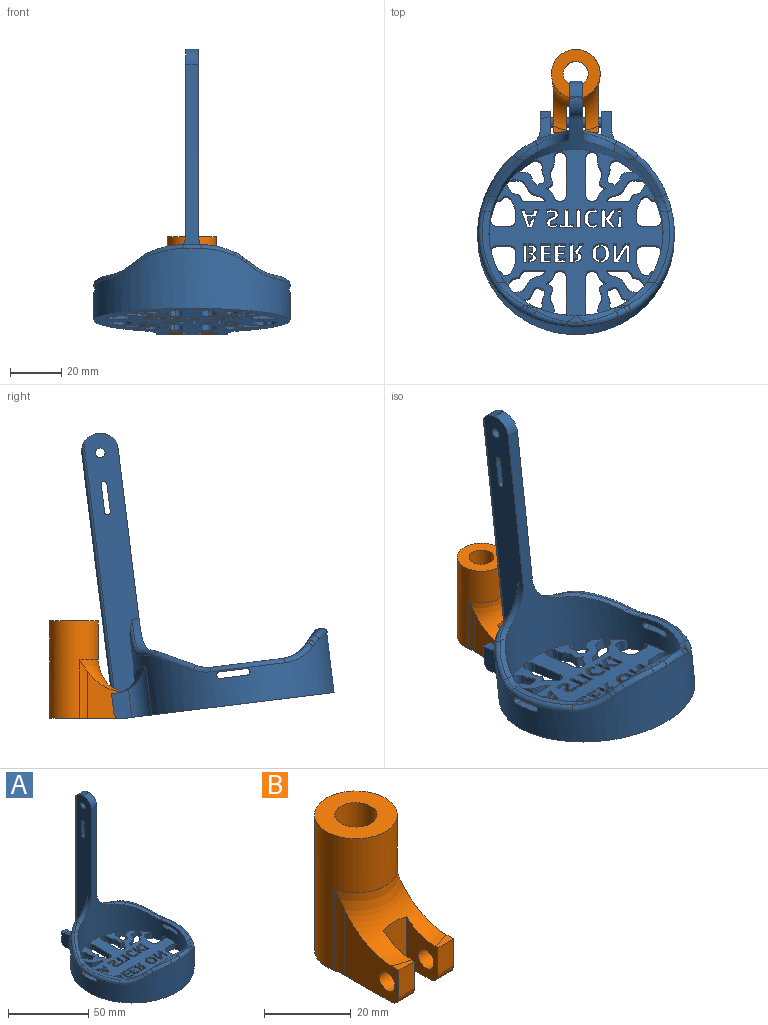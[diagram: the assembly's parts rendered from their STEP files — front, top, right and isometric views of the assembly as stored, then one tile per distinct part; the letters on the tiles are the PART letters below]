
ASSEMBLY  parts=2 mates=1
PART A: 362 faces, bbox 83.9x98.5x112.5 mm
  f0: plane 112.23x13.52mm, normal (-1,0,0), area 1224.4mm2, adj f3,f247,f253,f287,f289,f299,f302,f305
  f1: plane 112.23x13.52mm, normal (1,0,0), area 1226.5mm2, adj f3,f247,f253,f287,f296,f297,f298,f305
  f2: plane 6.78x2.6mm, normal (0,0,1), area 8.5mm2, adj f314,f320,f335
  f3: cylinder r=38.42mm len=76.84mm, axis (0,0,-1), area 3852.1mm2, adj f0,f1,f253,f297,f302,f303,f304,f326
  f4: plane 68.07x68.07mm, normal (0,0,1), area 2117.4mm2, adj f5,f6,f7,f8,f9,f10,f11,f12
  f5: extruded ~6.43x3.81mm, area 32.9mm2, adj f4,f225,f253,f283
  f6: extruded ~6.43x3.81mm, area 32.9mm2, adj f4,f7,f253,f282
  f7: extruded ~7.59x5.02mm, area 38.4mm2, adj f4,f6,f247,f253
  f8: extruded ~7.59x5.02mm, area 38.4mm2, adj f4,f226,f247,f253
  f9: extruded ~3.81x0.62mm, area 2.6mm2, adj f4,f10,f227,f253
  f10: extruded ~3.81x0.62mm, area 2.6mm2, adj f4,f9,f11,f253
  f11: extruded ~3.81x0.64mm, area 2.6mm2, adj f4,f10,f12,f253
  f12: extruded ~3.81x0.63mm, area 2.6mm2, adj f4,f11,f13,f253
  f13: extruded ~3.81x0.61mm, area 2.6mm2, adj f4,f12,f14,f253
  f14: extruded ~3.81x0.62mm, area 2.6mm2, adj f4,f13,f15,f253
  f15: extruded ~3.81x0.63mm, area 2.6mm2, adj f4,f14,f227,f253
  f16: plane 3.81x1.2mm, normal (0,-1,0), area 4.6mm2, adj f4,f17,f228,f253
  f17: plane 4.8x3.81mm, normal (-1,-0.05,0), area 18.3mm2, adj f4,f16,f18,f253
  f18: plane 3.81x1.7mm, normal (0,1,0), area 6.5mm2, adj f4,f17,f228,f253
  f19: plane 3.81x1.73mm, normal (0,-1,0), area 6.6mm2, adj f4,f20,f229,f253
  f20: plane 4x3.81mm, normal (-0.85,0.53,0), area 18mm2, adj f4,f19,f21,f253
  f21: plane 3.81x3.18mm, normal (-0.79,-0.62,0), area 15.4mm2, adj f4,f20,f22,f253
  f22: plane 3.81x1.69mm, normal (0,1,0), area 6.4mm2, adj f4,f21,f23,f253
  f23: plane 3.81x2.44mm, normal (0.78,0.62,0), area 11.9mm2, adj f4,f22,f24,f253
  f24: plane 3.81x0.85mm, normal (0.82,0.58,0), area 3.9mm2, adj f4,f23,f25,f253
  f25: plane 3.81x3.28mm, normal (-1,0,0), area 12.5mm2, adj f4,f24,f26,f253
  f26: plane 3.81x1.52mm, normal (0,1,0), area 5.8mm2, adj f4,f25,f27,f253
  f27: plane 7.18x3.81mm, normal (1,0,0), area 27.3mm2, adj f4,f26,f28,f253
  f28: plane 3.81x1.52mm, normal (0,-1,0), area 5.8mm2, adj f4,f27,f29,f253
  f29: plane 3.81x2.56mm, normal (-1,0,0), area 9.8mm2, adj f4,f28,f30,f253
  f30: plane 3.81x0.64mm, normal (-0.58,-0.81,0), area 3mm2, adj f4,f29,f229,f253
  f31: extruded ~3.81x1.33mm, area 5.9mm2, adj f4,f32,f230,f253
  f32: extruded ~3.81x0.8mm, area 3.1mm2, adj f4,f31,f33,f253
  f33: extruded ~3.81x0.81mm, area 3.3mm2, adj f4,f32,f34,f253
  f34: plane 3.81x1.24mm, normal (-0.93,-0.37,0), area 5.1mm2, adj f4,f33,f35,f253
  f35: extruded ~3.81x2.1mm, area 8.3mm2, adj f4,f34,f36,f253
  f36: extruded ~3.81x1.79mm, area 7.1mm2, adj f4,f35,f37,f253
  f37: extruded ~3.81x1.29mm, area 6.7mm2, adj f4,f36,f38,f253
  f38: extruded ~3.81x1.96mm, area 7.7mm2, adj f4,f37,f39,f253
  f39: extruded ~3.81x2.73mm, area 11.1mm2, adj f4,f38,f40,f253
  f40: extruded ~3.81x2.4mm, area 10.1mm2, adj f4,f39,f41,f253
  f41: extruded ~3.81x1.97mm, area 7.7mm2, adj f4,f40,f42,f253
  f42: plane 3.81x1.28mm, normal (-1,0,0), area 4.9mm2, adj f4,f41,f43,f253
  f43: extruded ~3.81x1.83mm, area 7.1mm2, adj f4,f42,f44,f253
  f44: extruded ~3.81x2.4mm, area 13mm2, adj f4,f43,f230,f253
  f45: plane 7.18x3.81mm, normal (1,0,0), area 27.3mm2, adj f4,f46,f231,f253
  f46: plane 3.81x1.52mm, normal (0,-1,0), area 5.8mm2, adj f4,f45,f47,f253
  f47: plane 7.18x3.81mm, normal (-1,0,0), area 27.3mm2, adj f4,f46,f231,f253
  f48: plane 3.81x1.52mm, normal (0,-1,0), area 5.8mm2, adj f4,f49,f232,f253
  f49: plane 5.91x3.81mm, normal (-1,0,0), area 22.5mm2, adj f4,f48,f50,f253
  f50: plane 3.81x1.95mm, normal (0,-1,0), area 7.4mm2, adj f4,f49,f51,f253
  f51: plane 3.81x1.27mm, normal (-1,0,0), area 4.8mm2, adj f4,f50,f52,f253
  f52: plane 5.42x3.81mm, normal (0,1,0), area 20.6mm2, adj f4,f51,f53,f253
  f53: plane 3.81x1.27mm, normal (1,0,0), area 4.8mm2, adj f4,f52,f54,f253
  f54: plane 3.81x1.95mm, normal (0,-1,0), area 7.4mm2, adj f4,f53,f232,f253
  f55: extruded ~3.81x1.53mm, area 6.7mm2, adj f4,f56,f233,f253
  f56: extruded ~3.81x1.19mm, area 4.8mm2, adj f4,f55,f57,f253
  f57: extruded ~3.81x1.38mm, area 6.5mm2, adj f4,f56,f58,f253
  f58: extruded ~3.81x0.96mm, area 4.1mm2, adj f4,f57,f59,f253
  f59: extruded ~3.81x0.3mm, area 1.6mm2, adj f4,f58,f60,f253
  f60: extruded ~3.81x0.35mm, area 1.4mm2, adj f4,f59,f61,f253
  f61: extruded ~3.81x0.52mm, area 2.3mm2, adj f4,f60,f62,f253
  f62: extruded ~3.81x0.66mm, area 2.7mm2, adj f4,f61,f63,f253
  f63: extruded ~3.81x0.74mm, area 2.8mm2, adj f4,f62,f64,f253
  f64: extruded ~3.81x0.95mm, area 3.8mm2, adj f4,f63,f65,f253
  f65: plane 3.81x1.18mm, normal (-0.92,-0.38,0), area 4.9mm2, adj f4,f64,f66,f253
  f66: extruded ~3.81x1.06mm, area 4.3mm2, adj f4,f65,f67,f253
  f67: extruded ~3.81x1.07mm, area 4.1mm2, adj f4,f66,f68,f253
  f68: extruded ~3.81x1.78mm, area 7.3mm2, adj f4,f67,f69,f253
  f69: extruded ~3.81x1.5mm, area 6.4mm2, adj f4,f68,f70,f253
  f70: extruded ~3.81x0.88mm, area 3.5mm2, adj f4,f69,f71,f253
  f71: extruded ~3.81x0.66mm, area 3.2mm2, adj f4,f70,f72,f253
  f72: extruded ~3.81x0.99mm, area 4.4mm2, adj f4,f71,f73,f253
  f73: extruded ~3.81x0.93mm, area 4mm2, adj f4,f72,f74,f253
  f74: extruded ~3.81x0.35mm, area 1.8mm2, adj f4,f73,f75,f253
  f75: extruded ~3.81x0.38mm, area 1.5mm2, adj f4,f74,f76,f253
  f76: extruded ~3.81x0.57mm, area 2.5mm2, adj f4,f75,f77,f253
  f77: extruded ~3.81x0.77mm, area 3.1mm2, adj f4,f76,f78,f253
  f78: extruded ~3.81x0.92mm, area 3.6mm2, adj f4,f77,f79,f253
  f79: extruded ~3.81x1.23mm, area 5mm2, adj f4,f78,f80,f253
  f80: plane 3.81x1.41mm, normal (1,0,0), area 5.4mm2, adj f4,f79,f81,f253
  f81: extruded ~3.81x2.03mm, area 8mm2, adj f4,f80,f233,f253
  f82: plane 3.81x1.71mm, normal (-0.96,-0.29,0), area 6.8mm2, adj f4,f83,f234,f253
  f83: plane 3.81x2.62mm, normal (0,-1,0), area 10mm2, adj f4,f82,f84,f253
  f84: plane 3.81x1.71mm, normal (0.96,-0.29,0), area 6.8mm2, adj f4,f83,f85,f253
  f85: plane 3.81x1.64mm, normal (0,-1,0), area 6.2mm2, adj f4,f84,f86,f253
  f86: plane 3.81x3.02mm, normal (-0.94,0.33,0), area 12.2mm2, adj f4,f85,f87,f253
  f87: plane 3.81x1.47mm, normal (0,1,0), area 5.6mm2, adj f4,f86,f88,f253
  f88: plane 3.81x0.04mm, normal (0.96,-0.3,0), area 0.2mm2, adj f4,f87,f89,f253
  f89: plane 3.81x1.87mm, normal (0,1,0), area 7.1mm2, adj f4,f88,f90,f253
  f90: extruded ~3.81x3.11mm, area 12.4mm2, adj f4,f89,f91,f253
  f91: extruded ~3.81x0.48mm, area 1.9mm2, adj f4,f90,f92,f253
  f92: extruded ~3.81x2.08mm, area 8.3mm2, adj f4,f91,f93,f253
  f93: plane 3.81x1.45mm, normal (0,-1,0), area 5.5mm2, adj f4,f92,f94,f253
  f94: plane 3.81x3.67mm, normal (-0.94,0.33,0), area 14.8mm2, adj f4,f93,f95,f253
  f95: plane 3.81x1.86mm, normal (0,1,0), area 7.1mm2, adj f4,f94,f96,f253
  f96: plane 7.21x3.81mm, normal (0.94,0.33,0), area 29.1mm2, adj f4,f95,f234,f253
  f97: plane 3.81x1.93mm, normal (0,-1,0), area 7.4mm2, adj f4,f98,f235,f253
  f98: plane 7.18x3.81mm, normal (-1,0,0), area 27.3mm2, adj f4,f97,f99,f253
  f99: plane 3.81x1.37mm, normal (0,1,0), area 5.2mm2, adj f4,f98,f100,f253
  f100: plane 3.81x3.4mm, normal (1,0,0), area 12.9mm2, adj f4,f99,f101,f253
  f101: extruded ~3.81x1.98mm, area 7.5mm2, adj f4,f100,f102,f253
  f102: plane 3.81x0.03mm, normal (0,1,0), area 0.1mm2, adj f4,f101,f103,f253
  f103: plane 5.37x3.81mm, normal (-0.87,0.5,0), area 23.7mm2, adj f4,f102,f104,f253
  f104: plane 3.81x1.92mm, normal (0,1,0), area 7.3mm2, adj f4,f103,f105,f253
  f105: plane 7.18x3.81mm, normal (1,0,0), area 27.3mm2, adj f4,f104,f106,f253
  f106: plane 3.81x1.36mm, normal (0,-1,0), area 5.2mm2, adj f4,f105,f107,f253
  f107: plane 3.81x3.38mm, normal (-1,0,0), area 12.9mm2, adj f4,f106,f108,f253
  f108: extruded ~3.81x2.05mm, area 7.8mm2, adj f4,f107,f109,f253
  f109: plane 3.81x0.04mm, normal (0,-1,0), area 0.2mm2, adj f4,f108,f235,f253
  f110: plane 4.13x3.81mm, normal (0,-1,0), area 15.7mm2, adj f4,f111,f236,f253
  f111: plane 3.81x1.26mm, normal (-1,0,0), area 4.8mm2, adj f4,f110,f112,f253
  f112: plane 3.81x2.61mm, normal (0,1,0), area 9.9mm2, adj f4,f111,f113,f253
  f113: plane 3.81x1.85mm, normal (-1,0,0), area 7mm2, adj f4,f112,f114,f253
  f114: plane 3.81x2.43mm, normal (0,-1,0), area 9.3mm2, adj f4,f113,f115,f253
  f115: plane 3.81x1.25mm, normal (-1,0,0), area 4.8mm2, adj f4,f114,f116,f253
  f116: plane 3.81x2.43mm, normal (0,1,0), area 9.3mm2, adj f4,f115,f117,f253
  f117: plane 3.81x1.58mm, normal (-1,0,0), area 6mm2, adj f4,f116,f118,f253
  f118: plane 3.81x2.61mm, normal (0,-1,0), area 9.9mm2, adj f4,f117,f119,f253
  f119: plane 3.81x1.25mm, normal (-1,0,0), area 4.8mm2, adj f4,f118,f120,f253
  f120: plane 4.13x3.81mm, normal (0,1,0), area 15.7mm2, adj f4,f119,f236,f253
  f121: plane 4.13x3.81mm, normal (0,-1,0), area 15.7mm2, adj f4,f122,f237,f253
  f122: plane 3.81x1.26mm, normal (-1,0,0), area 4.8mm2, adj f4,f121,f123,f253
  f123: plane 3.81x2.61mm, normal (0,1,0), area 9.9mm2, adj f4,f122,f124,f253
  f124: plane 3.81x1.85mm, normal (-1,0,0), area 7mm2, adj f4,f123,f125,f253
  f125: plane 3.81x2.43mm, normal (0,-1,0), area 9.3mm2, adj f4,f124,f126,f253
  f126: plane 3.81x1.25mm, normal (-1,0,0), area 4.8mm2, adj f4,f125,f127,f253
  f127: plane 3.81x2.43mm, normal (0,1,0), area 9.3mm2, adj f4,f126,f128,f253
  f128: plane 3.81x1.58mm, normal (-1,0,0), area 6mm2, adj f4,f127,f129,f253
  f129: plane 3.81x2.61mm, normal (0,-1,0), area 9.9mm2, adj f4,f128,f130,f253
  f130: plane 3.81x1.25mm, normal (-1,0,0), area 4.8mm2, adj f4,f129,f131,f253
  f131: plane 4.13x3.81mm, normal (0,1,0), area 15.7mm2, adj f4,f130,f237,f253
  f132: plane 3.81x1.26mm, normal (1,0,0), area 4.8mm2, adj f4,f133,f238,f253
  f133: plane 3.81x0.66mm, normal (0,-1,0), area 2.5mm2, adj f4,f132,f134,f253
  f134: extruded ~3.81x1.93mm, area 7.8mm2, adj f4,f133,f135,f253
  f135: extruded ~3.81x1.53mm, area 6.7mm2, adj f4,f134,f136,f253
  f136: extruded ~3.81x1.11mm, area 4.5mm2, adj f4,f135,f137,f253
  f137: extruded ~3.81x0.98mm, area 4.4mm2, adj f4,f136,f138,f253
  f138: plane 3.81x0.05mm, normal (-1,0,0), area 0.2mm2, adj f4,f137,f139,f253
  f139: extruded ~3.81x0.8mm, area 3.7mm2, adj f4,f138,f140,f253
  f140: extruded ~3.81x1.06mm, area 4.3mm2, adj f4,f139,f141,f253
  f141: extruded ~3.81x1.38mm, area 6.2mm2, adj f4,f140,f142,f253
  f142: extruded ~3.81x2.22mm, area 8.7mm2, adj f4,f141,f143,f253
  f143: plane 3.81x0.21mm, normal (0,1,0), area 0.8mm2, adj f4,f142,f144,f253
  f144: plane 3.81x1.25mm, normal (1,0,0), area 4.8mm2, adj f4,f143,f145,f253
  f145: plane 3.81x0.3mm, normal (0,-1,0), area 1.1mm2, adj f4,f144,f146,f253
  f146: extruded ~3.81x0.96mm, area 3.7mm2, adj f4,f145,f147,f253
  f147: extruded ~3.81x0.59mm, area 2.7mm2, adj f4,f146,f148,f253
  f148: extruded ~3.81x0.63mm, area 2.7mm2, adj f4,f147,f149,f253
  f149: extruded ~3.81x0.9mm, area 3.5mm2, adj f4,f148,f150,f253
  f150: plane 3.81x0.38mm, normal (0,1,0), area 1.5mm2, adj f4,f149,f151,f253
  f151: plane 3.81x1.21mm, normal (1,0,0), area 4.6mm2, adj f4,f150,f152,f253
  f152: plane 3.81x0.44mm, normal (0,-1,0), area 1.7mm2, adj f4,f151,f153,f253
  f153: extruded ~3.81x1.28mm, area 6.7mm2, adj f4,f152,f154,f253
  f154: extruded ~3.81x0.74mm, area 3.1mm2, adj f4,f153,f155,f253
  f155: extruded ~3.81x0.93mm, area 3.7mm2, adj f4,f154,f238,f253
  f156: plane 3.81x0.02mm, normal (0,1,0), area 0.1mm2, adj f4,f157,f239,f253
  f157: plane 3.81x1.25mm, normal (1,0,0), area 4.8mm2, adj f4,f156,f158,f253
  f158: extruded ~3.81x1mm, area 3.9mm2, adj f4,f157,f159,f253
  f159: extruded ~3.81x0.73mm, area 3.2mm2, adj f4,f158,f160,f253
  f160: extruded ~3.81x0.76mm, area 3.3mm2, adj f4,f159,f161,f253
  f161: extruded ~3.81x1.07mm, area 4.2mm2, adj f4,f160,f162,f253
  f162: plane 3.81x0.49mm, normal (0,1,0), area 1.9mm2, adj f4,f161,f163,f253
  f163: plane 3.81x1.94mm, normal (-1,0,0), area 7.4mm2, adj f4,f162,f164,f253
  f164: plane 3.81x0.04mm, normal (0,-1,0), area 0.2mm2, adj f4,f163,f165,f253
  f165: plane 3.81x1.25mm, normal (-1,0,0), area 4.8mm2, adj f4,f164,f166,f253
  f166: plane 3.81x1.57mm, normal (0,1,0), area 6mm2, adj f4,f165,f167,f253
  f167: plane 7.18x3.81mm, normal (1,0,0), area 27.3mm2, adj f4,f166,f168,f253
  f168: plane 3.81x1.52mm, normal (0,-1,0), area 5.8mm2, adj f4,f167,f169,f253
  f169: plane 3.81x2.75mm, normal (-1,0,0), area 10.5mm2, adj f4,f168,f170,f253
  f170: plane 3.81x0.81mm, normal (0,-1,0), area 3.1mm2, adj f4,f169,f171,f253
  f171: plane 3.81x2.75mm, normal (0.85,-0.53,0), area 12.4mm2, adj f4,f170,f172,f253
  f172: plane 3.81x1.69mm, normal (0,-1,0), area 6.4mm2, adj f4,f171,f173,f253
  f173: extruded ~3.81x3.13mm, area 14.4mm2, adj f4,f172,f174,f253
  f174: extruded ~3.81x0.99mm, area 4.8mm2, adj f4,f173,f175,f253
  f175: extruded ~3.81x1.13mm, area 4.6mm2, adj f4,f174,f176,f253
  f176: extruded ~3.81x1.62mm, area 7mm2, adj f4,f175,f239,f253
  f177: plane 3.81x1.3mm, normal (-1,0,0), area 5mm2, adj f4,f178,f240,f253
  f178: extruded ~3.81x2.03mm, area 8.7mm2, adj f4,f177,f179,f253
  f179: extruded ~3.81x2.74mm, area 11.2mm2, adj f4,f178,f180,f253
  f180: extruded ~3.81x2.75mm, area 11.3mm2, adj f4,f179,f181,f253
  f181: extruded ~3.81x2.03mm, area 8.7mm2, adj f4,f180,f182,f253
  f182: plane 3.81x1.31mm, normal (-1,0,0), area 5mm2, adj f4,f181,f183,f253
  f183: extruded ~3.81x0.86mm, area 4mm2, adj f4,f182,f184,f253
  f184: extruded ~3.81x1.81mm, area 7.2mm2, adj f4,f183,f185,f253
  f185: extruded ~3.81x1.81mm, area 7.2mm2, adj f4,f184,f240,f253
  f186: extruded ~3.81x3.7mm, area 19.4mm2, adj f4,f241,f253,f267
  f187: plane 14.84x3.81mm, normal (-1,0,0), area 56.5mm2, adj f4,f253,f266,f277
  f188: extruded ~5.3x5.13mm, area 30.3mm2, adj f4,f247,f253,f265
  f189: plane 7.6x3.81mm, normal (0,-1,0), area 29mm2, adj f4,f190,f253,f265
  f190: extruded ~14.22x8.64mm, area 68.5mm2, adj f4,f189,f247,f253
  f191: plane 3.81x3.55mm, normal (-1,0,0), area 13.5mm2, adj f4,f192,f253,f264
  f192: extruded ~7.51x5.86mm, area 44.7mm2, adj f4,f191,f247,f253
  f193: plane 3.81x3.55mm, normal (-1,0,0), area 13.5mm2, adj f4,f243,f253,f263
  f194: plane 4.84x3.81mm, normal (0,1,0), area 18.4mm2, adj f4,f253,f263,f274
  f195: plane 14.84x3.81mm, normal (1,0,0), area 56.5mm2, adj f4,f253,f260,f273
  f196: extruded ~11.82x3.81mm, area 52.5mm2, adj f4,f244,f253,f272
  f197: plane 7.6x3.81mm, normal (0,1,0), area 29mm2, adj f4,f198,f253,f259
  f198: extruded ~14.22x8.64mm, area 68.5mm2, adj f4,f197,f247,f253
  f199: extruded ~3.81x3.7mm, area 19.4mm2, adj f4,f200,f253,f268
  f200: extruded ~11.82x3.81mm, area 52.5mm2, adj f4,f199,f253,f278
  f201: plane 4.84x3.81mm, normal (0,1,0), area 18.4mm2, adj f4,f253,f258,f281
  f202: plane 3.81x3.55mm, normal (1,0,0), area 13.5mm2, adj f4,f203,f253,f258
  f203: extruded ~7.51x5.86mm, area 44.7mm2, adj f4,f202,f247,f253
  f204: extruded ~7.51x5.86mm, area 44.7mm2, adj f4,f205,f247,f253
  f205: plane 3.81x3.55mm, normal (1,0,0), area 13.5mm2, adj f4,f204,f253,f257
  f206: plane 4.84x3.81mm, normal (0,-1,0), area 18.4mm2, adj f4,f253,f257,f280
  f207: extruded ~14.22x8.64mm, area 68.5mm2, adj f4,f208,f247,f253
  f208: plane 7.6x3.81mm, normal (0,-1,0), area 29mm2, adj f4,f207,f253,f256
  f209: extruded ~5.3x5.13mm, area 30.3mm2, adj f4,f247,f253,f256
  f210: plane 3.81x1.51mm, normal (0,-1,0), area 5.8mm2, adj f4,f211,f248,f253
  f211: plane 7.18x3.81mm, normal (-1,0,0), area 27.3mm2, adj f4,f210,f212,f253
  f212: plane 3.81x1.51mm, normal (0,1,0), area 5.8mm2, adj f4,f211,f248,f253
  f213: extruded ~3.81x2.52mm, area 10.6mm2, adj f4,f214,f249,f253
  f214: plane 3.81x1.27mm, normal (1,0,0), area 4.8mm2, adj f4,f213,f215,f253
  f215: extruded ~3.81x2.42mm, area 13.1mm2, adj f4,f214,f216,f253
  f216: extruded ~3.81x2.42mm, area 13.1mm2, adj f4,f215,f217,f253
  f217: plane 3.81x1.28mm, normal (1,0,0), area 4.9mm2, adj f4,f216,f218,f253
  f218: extruded ~3.81x2.51mm, area 10.6mm2, adj f4,f217,f219,f253
  f219: extruded ~3.81x2.74mm, area 11.2mm2, adj f4,f218,f249,f253
  f220: extruded ~7.59x5.02mm, area 38.4mm2, adj f4,f247,f250,f253
  f221: extruded ~3.81x3.7mm, area 19.4mm2, adj f4,f222,f253,f255
  f222: extruded ~11.82x3.81mm, area 52.5mm2, adj f4,f221,f253,f270
  f223: extruded ~14.22x8.64mm, area 68.5mm2, adj f4,f224,f247,f253
  f224: plane 7.6x3.81mm, normal (0,1,0), area 29mm2, adj f4,f223,f253,f262
  f225: extruded ~7.59x5.02mm, area 38.4mm2, adj f4,f5,f247,f253
  f226: extruded ~6.43x3.81mm, area 32.9mm2, adj f4,f8,f253,f285
  f227: extruded ~3.81x0.64mm, area 2.6mm2, adj f4,f9,f15,f253
  f228: plane 4.8x3.81mm, normal (1,-0.05,0), area 18.3mm2, adj f4,f16,f18,f253
  f229: plane 3.81x3.02mm, normal (0.85,-0.53,0), area 13.6mm2, adj f4,f19,f30,f253
  f230: extruded ~3.81x1.8mm, area 7.2mm2, adj f4,f31,f44,f253
  f231: plane 3.81x1.52mm, normal (0,1,0), area 5.8mm2, adj f4,f45,f47,f253
  f232: plane 5.91x3.81mm, normal (1,0,0), area 22.5mm2, adj f4,f48,f54,f253
  f233: extruded ~3.81x1.95mm, area 7.9mm2, adj f4,f55,f81,f253
  f234: plane 3.81x1.64mm, normal (0,-1,0), area 6.2mm2, adj f4,f82,f96,f253
  f235: plane 5.43x3.81mm, normal (0.87,-0.5,0), area 23.9mm2, adj f4,f97,f109,f253
  f236: plane 7.18x3.81mm, normal (1,0,0), area 27.3mm2, adj f4,f110,f120,f253
  f237: plane 7.18x3.81mm, normal (1,0,0), area 27.3mm2, adj f4,f121,f131,f253
  f238: plane 3.81x0.49mm, normal (0,1,0), area 1.9mm2, adj f4,f132,f155,f253
  f239: extruded ~3.81x2.17mm, area 8.6mm2, adj f4,f156,f176,f253
  f240: extruded ~3.81x0.86mm, area 4mm2, adj f4,f177,f185,f253
  f241: extruded ~11.82x3.81mm, area 52.5mm2, adj f4,f186,f253,f276
  f242: plane 4.84x3.81mm, normal (0,-1,0), area 18.4mm2, adj f4,f253,f264,f275
  f243: extruded ~7.51x5.86mm, area 44.7mm2, adj f4,f193,f247,f253
  f244: extruded ~3.81x3.7mm, area 19.4mm2, adj f4,f196,f253,f261
  f245: extruded ~5.3x5.13mm, area 30.3mm2, adj f4,f247,f253,f259
  f246: plane 14.84x3.81mm, normal (1,0,0), area 56.5mm2, adj f4,f253,f269,f279
  f247: cylinder r=34.04mm len=104.9mm, axis (0,0,-1), area 4119.4mm2, adj f0,f1,f4,f7,f8,f188,f190,f192
  f248: plane 7.18x3.81mm, normal (1,0,0), area 27.3mm2, adj f4,f210,f212,f253
  f249: extruded ~3.81x2.74mm, area 11.2mm2, adj f4,f213,f219,f253
  f250: extruded ~6.43x3.81mm, area 32.9mm2, adj f4,f220,f253,f284
  f251: plane 14.84x3.81mm, normal (-1,0,0), area 56.5mm2, adj f4,f253,f254,f271
  f252: extruded ~5.3x5.13mm, area 30.3mm2, adj f4,f247,f253,f262
  f253: plane 84.14x76.84mm, normal (0,0,-1), area 3244.7mm2, adj f0,f1,f3,f5,f6,f7,f8,f9
  f254: cylinder r=2.54mm len=3.81mm, axis (0,0,-1), area 14.9mm2, adj f4,f251,f253,f255
  f255: cylinder r=2.54mm len=3.81mm, axis (0,0,-1), area 11.2mm2, adj f4,f221,f253,f254
  f256: cylinder r=2.54mm len=3.81mm, axis (0,0,-1), area 13mm2, adj f4,f208,f209,f253
  f257: cylinder r=2.54mm len=3.81mm, axis (0,0,1), area 15.2mm2, adj f4,f205,f206,f253
  f258: cylinder r=2.54mm len=3.81mm, axis (0,0,-1), area 15.2mm2, adj f4,f201,f202,f253
  f259: cylinder r=2.54mm len=3.81mm, axis (0,0,-1), area 13mm2, adj f4,f197,f245,f253
  f260: cylinder r=2.54mm len=3.81mm, axis (0,0,1), area 14.9mm2, adj f4,f195,f253,f261
  f261: cylinder r=2.54mm len=3.81mm, axis (0,0,-1), area 11.2mm2, adj f4,f244,f253,f260
  f262: cylinder r=2.54mm len=3.81mm, axis (0,0,-1), area 13mm2, adj f4,f224,f252,f253
  f263: cylinder r=2.54mm len=3.81mm, axis (0,0,-1), area 15.2mm2, adj f4,f193,f194,f253
  f264: cylinder r=2.54mm len=3.81mm, axis (0,0,1), area 15.2mm2, adj f4,f191,f242,f253
  f265: cylinder r=2.54mm len=3.81mm, axis (0,0,-1), area 13mm2, adj f4,f188,f189,f253
  f266: cylinder r=2.54mm len=3.81mm, axis (0,0,-1), area 14.9mm2, adj f4,f187,f253,f267
  f267: cylinder r=2.54mm len=3.81mm, axis (0,0,-1), area 11.2mm2, adj f4,f186,f253,f266
  f268: cylinder r=2.54mm len=3.81mm, axis (0,0,-1), area 11.2mm2, adj f4,f199,f253,f269
  f269: cylinder r=2.54mm len=3.81mm, axis (0,0,1), area 14.9mm2, adj f4,f246,f253,f268
  f270: cylinder r=2.54mm len=3.81mm, axis (0,0,-1), area 14mm2, adj f4,f222,f253,f271
  f271: cylinder r=2.54mm len=3.81mm, axis (0,0,-1), area 16.6mm2, adj f4,f251,f253,f270
  f272: cylinder r=2.54mm len=3.81mm, axis (0,0,-1), area 14mm2, adj f4,f196,f253,f273
  f273: cylinder r=2.54mm len=3.81mm, axis (0,0,-1), area 16.6mm2, adj f4,f195,f253,f272
  f274: cylinder r=2.54mm len=3.81mm, axis (0,0,-1), area 17.2mm2, adj f4,f194,f247,f253
  f275: cylinder r=2.54mm len=3.81mm, axis (0,0,-1), area 17.2mm2, adj f4,f242,f247,f253
  f276: cylinder r=2.54mm len=3.81mm, axis (0,0,-1), area 14mm2, adj f4,f241,f253,f277
  f277: cylinder r=2.54mm len=3.81mm, axis (0,0,-1), area 16.6mm2, adj f4,f187,f253,f276
  f278: cylinder r=2.54mm len=3.81mm, axis (0,0,-1), area 14mm2, adj f4,f200,f253,f279
  f279: cylinder r=2.54mm len=3.81mm, axis (0,0,-1), area 16.6mm2, adj f4,f246,f253,f278
  f280: cylinder r=2.54mm len=3.81mm, axis (0,0,-1), area 17.2mm2, adj f4,f206,f247,f253
  f281: cylinder r=2.54mm len=3.81mm, axis (0,0,-1), area 17.2mm2, adj f4,f201,f247,f253
  f282: cylinder r=2.54mm len=3.81mm, axis (0,0,-1), area 22.9mm2, adj f4,f6,f247,f253
  f283: cylinder r=2.54mm len=3.81mm, axis (0,0,-1), area 22.9mm2, adj f4,f5,f247,f253
  f284: cylinder r=2.54mm len=3.81mm, axis (0,0,-1), area 22.9mm2, adj f4,f247,f250,f253
  f285: cylinder r=2.54mm len=3.81mm, axis (0,0,-1), area 22.9mm2, adj f4,f226,f247,f253
  f286: plane 102.36x2.54mm, normal (0,1,0), area 260mm2, adj f306,f307,f345,f346
  f287: plane 5.08x0.59mm, normal (0,0,1), area 2.7mm2, adj f0,f1,f305,f306
  f288: plane 3.81x3.06mm, normal (0,0,1), area 9.6mm2, adj f290,f291,f292,f302
  f289: plane 17.21x7.97mm, normal (0,1,0), area 118.4mm2, adj f0,f253,f290,f302
  f290: plane 14.2x9.76mm, normal (1,0,0), area 94.2mm2, adj f253,f288,f289,f291,f299,f301,f302
  f291: plane 7.62x3.81mm, normal (0,1,0), area 29mm2, adj f288,f290,f292,f301
  f292: plane 10.94x6.87mm, normal (-1,0,0), area 69.1mm2, adj f253,f288,f291,f301,f302,f303
  f293: plane 10.16x6.84mm, normal (1,0,0), area 68.1mm2, adj f253,f294,f297,f300,f304
  f294: plane 7.62x3.81mm, normal (0,1,0), area 29mm2, adj f293,f295,f297,f300
  f295: plane 10.16x9.65mm, normal (-1,0,0), area 85.3mm2, adj f253,f294,f296,f297,f298,f300
  f296: plane 10.16x7.62mm, normal (0,1,0), area 77.4mm2, adj f1,f253,f295,f297
  f297: plane 16.02x14.63mm, normal (0,0,1), area 56.1mm2, adj f1,f3,f293,f294,f295,f296,f304
  f298: cylinder r=1.91mm len=7.62mm, axis (-1,0,0), area 91.2mm2, adj f1,f295
  f299: cylinder r=1.91mm len=7.62mm, axis (-1,0,0), area 91.2mm2, adj f0,f290
  f300: cylinder r=2.54mm len=3.81mm, axis (-1,0,0), area 15.2mm2, adj f253,f293,f294,f295
  f301: cylinder r=2.54mm len=3.81mm, axis (-1,0,0), area 15.2mm2, adj f253,f290,f291,f292
  f302: torus R=47.31mm, axis (0,0,1), area 109.1mm2, adj f0,f3,f288,f289,f290,f292,f303
  f303: cylinder r=8.89mm len=19.05mm, axis (0,0,-1), area 142.1mm2, adj f3,f253,f292,f302
  f304: cylinder r=8.89mm len=10.16mm, axis (0,0,-1), area 96.3mm2, adj f3,f253,f293,f297
  f305: torus R=40.89mm, axis (0,0,1), area 53.7mm2, adj f0,f1,f247,f287
  f306: cylinder r=6.86mm len=6.86mm, axis (1,0,0), area 49.3mm2, adj f0,f1,f286,f287,f345,f346
  f307: cylinder r=2.54mm len=5.08mm, axis (-1,0,0), area 16.9mm2, adj f0,f1,f253,f286,f345,f346
  f308: plane 27.94x8.93mm, normal (0,0,1), area 76.1mm2, adj f247,f316,f317,f340
  f309: plane 4.49x1.09mm, normal (0,0.75,0.66), area 4.1mm2, adj f247,f316,f319,f338
  f310: plane 14.58x14.58mm, normal (0,-0.45,0.89), area 42.1mm2, adj f247,f317,f318,f342
  f311: plane 27.94x8.93mm, normal (0,0,1), area 76.1mm2, adj f247,f322,f323,f330
  f312: plane 4.49x1.09mm, normal (0,0.75,0.66), area 4.1mm2, adj f247,f315,f322,f332
  f313: plane 14.58x14.58mm, normal (0,-0.45,0.89), area 42.1mm2, adj f247,f321,f323,f328
  f314: bspline ~18.49x10.49mm, area 34.8mm2, adj f2,f247,f315,f334
  f315: cylinder r=12.7mm len=2.96mm, axis (-1,0,0), area 3.7mm2, adj f312,f314,f333
  f316: cylinder r=12.7mm len=13.55mm, axis (-1,0,0), area 32mm2, adj f247,f308,f309,f339
  f317: cylinder r=12.7mm len=5.73mm, axis (1,0,0), area 15.4mm2, adj f247,f308,f310,f341
  f318: cylinder r=12.7mm len=7.75mm, axis (1,0,0), area 15.9mm2, adj f247,f310,f325,f343
  f319: cylinder r=12.7mm len=2.96mm, axis (-1,0,0), area 3.7mm2, adj f309,f320,f337
  f320: bspline ~16.37x9.79mm, area 34.8mm2, adj f2,f247,f319,f336
  f321: cylinder r=12.7mm len=7.75mm, axis (1,0,0), area 15.9mm2, adj f247,f313,f324,f327
  f322: cylinder r=12.7mm len=13.55mm, axis (-1,0,0), area 32mm2, adj f247,f311,f312,f331
  f323: cylinder r=12.7mm len=5.73mm, axis (1,0,0), area 15.4mm2, adj f247,f311,f313,f329
  f324: torus R=25.4mm, axis (1,0,0), area 59.7mm2, adj f1,f247,f321,f326
  f325: torus R=25.4mm, axis (1,0,0), area 59.7mm2, adj f0,f247,f318,f344
  f326: bspline ~17.73x15.17mm, area 46.2mm2, adj f1,f3,f324,f327
  f327: bspline ~12.15x8.9mm, area 30.7mm2, adj f3,f321,f326,f328
  f328: bspline ~19.76x15.41mm, area 63.9mm2, adj f3,f313,f327,f329
  f329: bspline ~10.17x4.93mm, area 20mm2, adj f3,f323,f328,f330
  f330: torus R=36.64mm, axis (0,0,-1), area 83.8mm2, adj f3,f311,f329,f331
  f331: bspline ~14.97x14.82mm, area 54.1mm2, adj f3,f322,f330,f332
  f332: bspline ~9.38x8.53mm, area 8.6mm2, adj f3,f312,f331,f333
  f333: bspline ~8.36x6.08mm, area 15.7mm2, adj f3,f315,f332,f334
  f334: bspline ~18.16x7.78mm, area 45.2mm2, adj f3,f314,f333,f335
  f335: torus R=36.64mm, axis (0,0,1), area 19.5mm2, adj f2,f3,f334,f336
  f336: bspline ~19.38x8.14mm, area 45.2mm2, adj f3,f320,f335,f337
  f337: bspline ~10.17x6.73mm, area 15.7mm2, adj f3,f319,f336,f338
  f338: bspline ~9.38x8.53mm, area 8.6mm2, adj f3,f309,f337,f339
  f339: bspline ~14.97x14.82mm, area 54.1mm2, adj f3,f316,f338,f340
  f340: torus R=36.64mm, axis (0,0,-1), area 83.8mm2, adj f3,f308,f339,f341
  f341: bspline ~8.99x4.4mm, area 20mm2, adj f3,f317,f340,f342
  f342: bspline ~19.76x15.41mm, area 63.9mm2, adj f3,f310,f341,f343
  f343: bspline ~12.15x8.9mm, area 30.7mm2, adj f3,f318,f342,f344
  f344: bspline ~17.73x15.17mm, area 46.2mm2, adj f0,f3,f325,f343
  f345: cylinder r=1.27mm len=108.54mm, axis (0,0,1), area 210.4mm2, adj f0,f286,f306,f307
  f346: cylinder r=1.27mm len=108.54mm, axis (0,0,-1), area 210.4mm2, adj f1,f286,f306,f307
  f347: plane 10.67x5.08mm, normal (0,1,0), area 54.2mm2, adj f0,f1,f359,f361
  f348: plane 10.67x5.08mm, normal (0,-1,0), area 54.2mm2, adj f0,f1,f358,f360
  f349: cylinder r=1.91mm len=5.08mm, axis (-1,0,0), area 60.8mm2, adj f0,f1
  f350: plane 10.67x4.8mm, normal (0,0,-1), area 46.9mm2, adj f3,f247,f356,f357
  f351: plane 10.67x4.8mm, normal (0,0,1), area 46.9mm2, adj f3,f247,f356,f357
  f352: plane 10.67x4.8mm, normal (0,0,1), area 46.9mm2, adj f3,f247,f354,f355
  f353: plane 10.67x4.8mm, normal (0,0,-1), area 46.9mm2, adj f3,f247,f354,f355
  f354: cylinder r=1.27mm len=4.66mm, axis (1,0,0), area 17.7mm2, adj f3,f247,f352,f353
  f355: cylinder r=1.27mm len=4.66mm, axis (-1,0,0), area 17.7mm2, adj f3,f247,f352,f353
  f356: cylinder r=1.27mm len=4.66mm, axis (1,0,0), area 17.7mm2, adj f3,f247,f350,f351
  f357: cylinder r=1.27mm len=4.66mm, axis (-1,0,0), area 17.7mm2, adj f3,f247,f350,f351
  f358: cylinder r=1.27mm len=5.08mm, axis (1,0,0), area 9.5mm2, adj f0,f1,f348,f359
  f359: cylinder r=1.27mm len=5.08mm, axis (-1,0,0), area 9.5mm2, adj f0,f1,f347,f358
  f360: cylinder r=1.27mm len=5.08mm, axis (-1,0,0), area 9.5mm2, adj f0,f1,f348,f361
  f361: cylinder r=1.27mm len=5.08mm, axis (1,0,0), area 9.5mm2, adj f0,f1,f347,f360
PART B: 22 faces, bbox 65.7x43.3x38.1 mm
  f0: cylinder r=9.53mm len=38.1mm, axis (0,0,-1), area 1685.8mm2, adj f3,f4,f17,f18,f19,f20,f21
  f1: cylinder r=4.86mm len=38.1mm, axis (0,0,-1), area 1149.6mm2, adj f3,f4,f20,f21
  f2: plane 5.08x2.49mm, normal (0,0,1), area 8.2mm2, adj f9,f10,f11,f18
  f3: plane 19.05x19.05mm, normal (0,0,1), area 210.7mm2, adj f0,f1
  f4: plane 29.85x19.05mm, normal (0,0,-1), area 374.6mm2, adj f0,f1,f5,f7,f8,f9,f11,f15
  f5: plane 18.39x17.59mm, normal (-1,0,0), area 196mm2, adj f4,f6,f12,f14,f15,f18,f19
  f6: plane 7.62x5.08mm, normal (0,-1,0), area 38.7mm2, adj f5,f7,f12,f15
  f7: plane 13.87x10.16mm, normal (1,0,0), area 92.2mm2, adj f4,f6,f8,f12,f14,f15,f18
  f8: plane 14.46x7.62mm, normal (0,-1,0), area 108.6mm2, adj f4,f7,f9,f18
  f9: plane 13.87x10.16mm, normal (-1,0,0), area 92.2mm2, adj f2,f4,f8,f10,f13,f16,f18
  f10: plane 7.62x5.08mm, normal (0,-1,0), area 38.7mm2, adj f2,f9,f11,f16
  f11: plane 18.39x17.59mm, normal (1,0,0), area 196mm2, adj f2,f4,f10,f13,f16,f17,f18
  f12: plane 5.08x2.49mm, normal (0,0,1), area 8.2mm2, adj f5,f6,f7,f18
  f13: cylinder r=2.54mm len=5.08mm, axis (-1,0,0), area 81.1mm2, adj f9,f11
  f14: cylinder r=2.54mm len=5.08mm, axis (-1,0,0), area 81.1mm2, adj f5,f7
  f15: cylinder r=2.54mm len=5.08mm, axis (1,0,0), area 20.3mm2, adj f4,f5,f6,f7
  f16: cylinder r=2.54mm len=5.08mm, axis (1,0,0), area 20.3mm2, adj f4,f9,f10,f11
  f17: cylinder r=12.7mm len=22.86mm, axis (0,0,-1), area 62.8mm2, adj f0,f4,f11,f18
  f18: torus R=22.23mm, axis (0,0,1), area 321.6mm2, adj f0,f2,f5,f7,f8,f9,f11,f12
  f19: cylinder r=12.7mm len=22.86mm, axis (0,0,-1), area 62.8mm2, adj f0,f4,f5,f18
  f20: cylinder r=1.52mm len=4.91mm, axis (0,1,0), area 45.2mm2, adj f0,f1
  f21: cylinder r=1.52mm len=4.91mm, axis (0,1,0), area 45.2mm2, adj f0,f1
PLACE A rot(axis=(-1,0,0),7deg) t=(0.08,-0.76,-2.29)mm
PLACE B at identity
MATE cylindrical A.f298 <-> B.f13  axis (-1,0,0) through (-10.08,-19.05,5.08)mm
